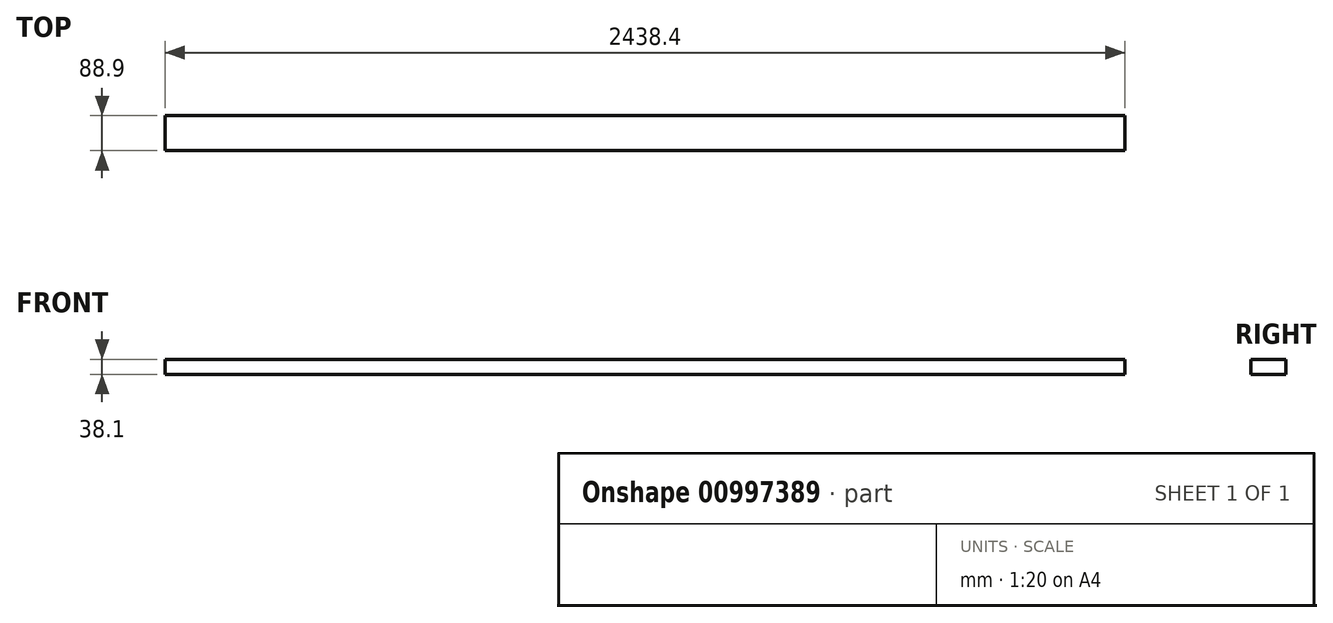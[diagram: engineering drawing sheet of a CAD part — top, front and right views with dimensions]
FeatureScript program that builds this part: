
annotation { "Feature Type Name" : "Feature", "Feature Type Description" : "" }
export const myFeature = defineFeature(function(context is Context, id is Id, definition is map)
    precondition{}
    {
        {
            var Q0;
            Q0=qCreatedBy(makeId("Right.planeOp"),FACE);
            var sketch = newSketch(context, id + "F0", { "sketchPlane" : qUnion([Q0])});
            skLineSegment(sketch, "E0.bottom", {"start": v(71.48, -9.84) * mm, "end": v(-17.42, -9.84) * mm});
            skLineSegment(sketch, "E0.top", {"start": v(71.48, -47.94) * mm, "end": v(-17.42, -47.94) * mm});
            skLineSegment(sketch, "E0.left", {"start": v(71.48, -9.84) * mm, "end": v(71.48, -47.94) * mm});
            skLineSegment(sketch, "E0.right", {"start": v(-17.42, -9.84) * mm, "end": v(-17.42, -47.94) * mm});
            skSolve(sketch);
        }
        {
            var Q0;
            Q0 = qSketchRegion(id + "F0", true);
            extrude(context, id + "F1", {"entities" : qUnion([Q0]), "depth" : 2438.4 * mm, "offsetDistance" : 25.4 * mm});
        }
    });
